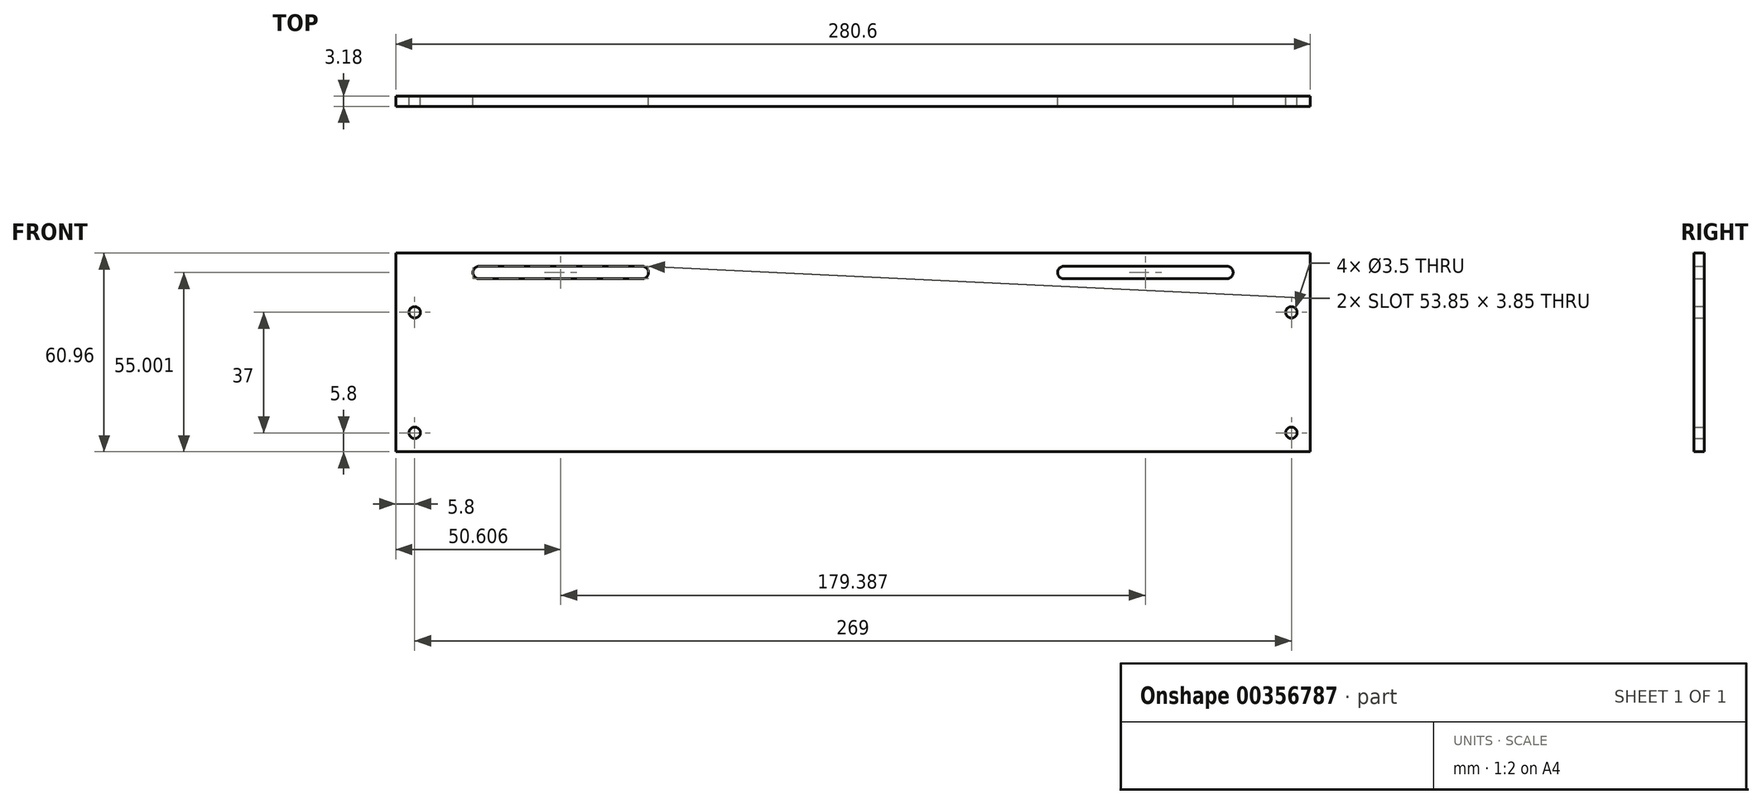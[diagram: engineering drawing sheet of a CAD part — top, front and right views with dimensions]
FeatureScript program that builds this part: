
annotation { "Feature Type Name" : "Feature", "Feature Type Description" : "" }
export const myFeature = defineFeature(function(context is Context, id is Id, definition is map)
    precondition{}
    {
        {
            var Q0;
            Q0=qCreatedBy(makeId("Front.planeOp"),FACE);
            var sketch = newSketch(context, id + "F0", { "sketchPlane" : qUnion([Q0])});
            skLineSegment(sketch, "E0.bottom", {"start": v(140.3, 30.48) * mm, "end": v(-140.3, 30.48) * mm});
            skLineSegment(sketch, "E0.top", {"start": v(140.3, -30.48) * mm, "end": v(-140.3, -30.48) * mm});
            skLineSegment(sketch, "E0.left", {"start": v(140.3, 30.48) * mm, "end": v(140.3, -30.48) * mm});
            skLineSegment(sketch, "E0.right", {"start": v(-140.3, 30.48) * mm, "end": v(-140.3, -30.48) * mm});
            skPoint(sketch, "E0.middle", {"position": v(0, 0) * mm});
            skCircle(sketch, "E1", {"center": v(-89.7, 24.52) * mm, "radius": 1.93 * mm});
            skLineSegment(sketch, "E2", {"start": v(-114.7, 24.52) * mm, "end": v(-64.7, 24.52) * mm});
            skArc(sketch, "E3.0.startCap", {"start": v(-114.7, 22.6) * mm, "mid": v(-116.62, 24.52) * mm, "end": v(-114.7, 26.45) * mm});
            skArc(sketch, "E3.0.endCap", {"start": v(-64.7, 26.45) * mm, "mid": v(-62.77, 24.52) * mm, "end": v(-64.7, 22.6) * mm});
            skLineSegment(sketch, "E3.0.left", {"start": v(-114.7, 26.45) * mm, "end": v(-64.7, 26.45) * mm});
            skLineSegment(sketch, "E3.0.right", {"start": v(-114.7, 22.6) * mm, "end": v(-64.7, 22.6) * mm});
            skArc(sketch, "E4.MirrorCS", {"start": v(64.7, 26.45) * mm, "mid": v(62.77, 24.52) * mm, "end": v(64.7, 22.6) * mm});
            skLineSegment(sketch, "E5.MirrorCS", {"start": v(114.7, 22.6) * mm, "end": v(64.7, 22.6) * mm});
            skArc(sketch, "E6.MirrorCS", {"start": v(114.7, 22.6) * mm, "mid": v(116.62, 24.52) * mm, "end": v(114.7, 26.45) * mm});
            skLineSegment(sketch, "E7.MirrorCS", {"start": v(114.7, 26.45) * mm, "end": v(64.7, 26.45) * mm});
            skPoint(sketch, "E8", {"position": v(89.7, 24.52) * mm});
            skPoint(sketch, "E8.positionSnap0", {"position": v(89.7, 26.45) * mm});
            skCircle(sketch, "E9", {"center": v(-134.5, -24.68) * mm, "radius": 1.75 * mm});
            skCircle(sketch, "E10", {"center": v(-134.5, 12.32) * mm, "radius": 1.75 * mm});
            skCircle(sketch, "E11.MirrorC", {"center": v(134.5, -24.68) * mm, "radius": 1.75 * mm});
            skCircle(sketch, "E12.MirrorC", {"center": v(134.5, 12.32) * mm, "radius": 1.75 * mm});
            skLineSegment(sketch, "E13", {"start": v(-134.5, -24.68) * mm, "end": v(-134.5, -30.48) * mm});
            skLineSegment(sketch, "E14", {"start": v(-134.5, -24.68) * mm, "end": v(-140.3, -24.68) * mm});
            skSolve(sketch);
        }
        {
            var Q0;
            Q0 = qSketchRegion(id + "F0", true);
            extrude(context, id + "F1", {"entities" : qUnion([Q0]), "endBound" : BoundingType.SYMMETRIC, "depth" : 3.17 * mm});
        }
    });
